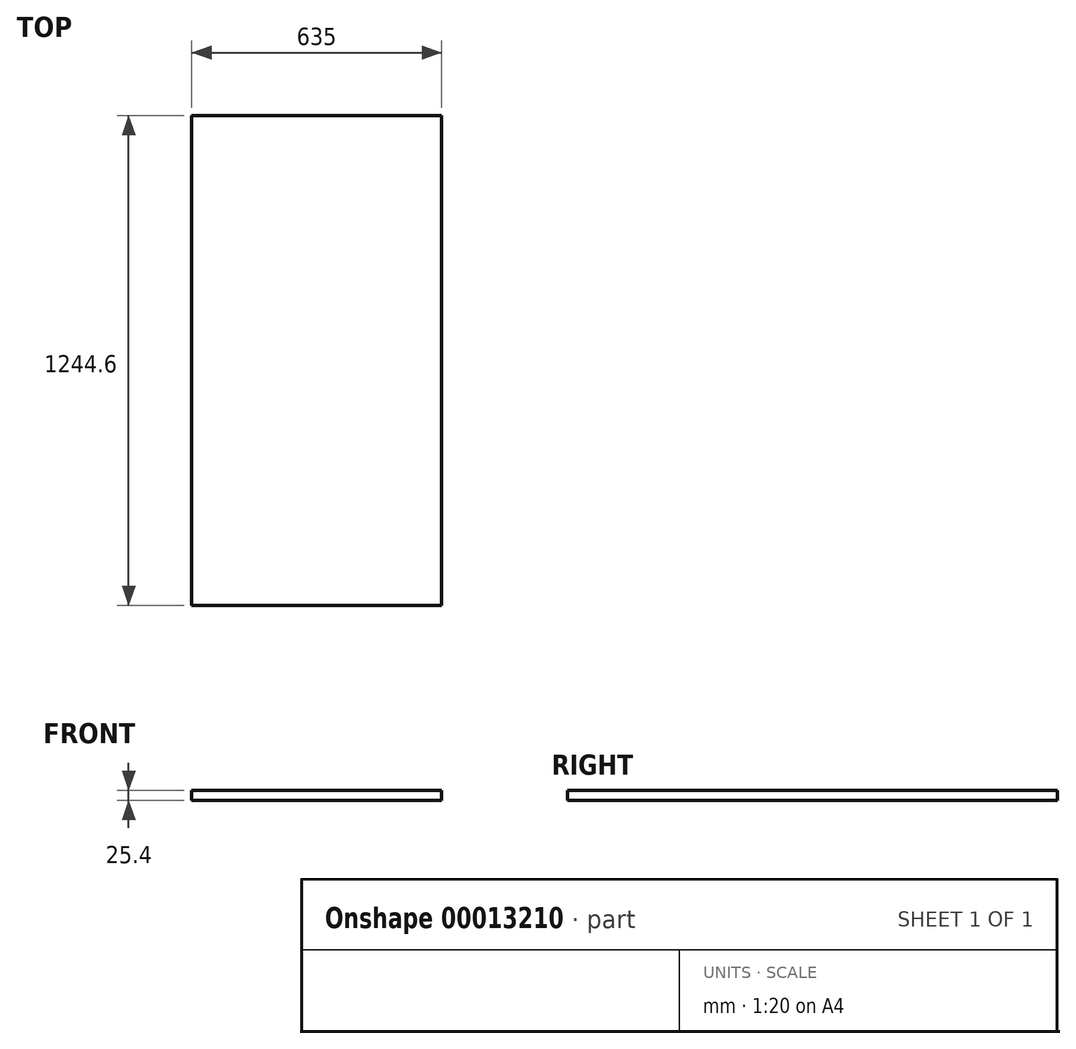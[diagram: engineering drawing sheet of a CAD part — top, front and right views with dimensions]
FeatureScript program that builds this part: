
annotation { "Feature Type Name" : "Feature", "Feature Type Description" : "" }
export const myFeature = defineFeature(function(context is Context, id is Id, definition is map)
    precondition{}
    {
        {
            var Q0;
            Q0=qCreatedBy(makeId("Top.planeOp"),FACE);
            var sketch = newSketch(context, id + "F0", { "sketchPlane" : qUnion([Q0])});
            skLineSegment(sketch, "E0.rect.bottom", {"start": v(317.5, -622.3) * mm, "end": v(-317.5, -622.3) * mm});
            skLineSegment(sketch, "E0.rect.top", {"start": v(317.5, 622.3) * mm, "end": v(-317.5, 622.3) * mm});
            skLineSegment(sketch, "E0.rect.left", {"start": v(317.5, -622.3) * mm, "end": v(317.5, 622.3) * mm});
            skLineSegment(sketch, "E0.rect.right", {"start": v(-317.5, -622.3) * mm, "end": v(-317.5, 622.3) * mm});
            skPoint(sketch, "E0.rect.middle", {"position": v(0, 0) * mm});
            skSolve(sketch);
        }
        {
            var Q0;
            Q0 = qSketchRegion(id + "F0", true);
            extrude(context, id + "F1", {"entities" : qUnion([Q0]), "depth" : 25.4 * mm});
        }
    });
